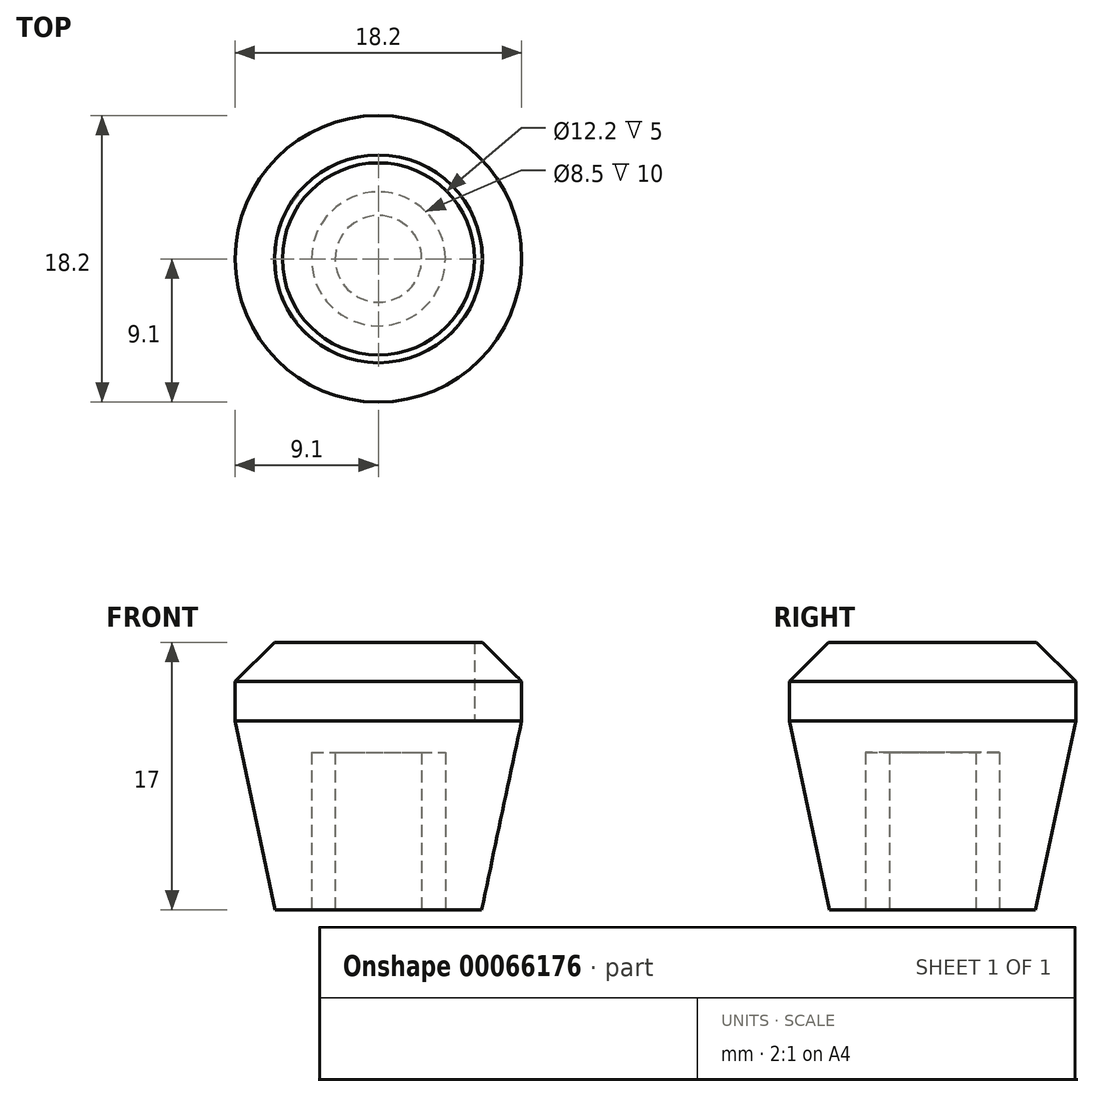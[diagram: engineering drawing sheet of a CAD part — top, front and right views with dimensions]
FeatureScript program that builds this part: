
annotation { "Feature Type Name" : "Feature", "Feature Type Description" : "" }
export const myFeature = defineFeature(function(context is Context, id is Id, definition is map)
    precondition{}
    {
        {
            assignVariable(context, id + "F0", {"variableType" : VariableType.NUMBER, "name" : "magt", "numberValue" : 5});
        }
        {
            var Q0;
            Q0=qCreatedBy(makeId("Top.planeOp"),FACE);
            var sketch = newSketch(context, id + "F1", { "sketchPlane" : qUnion([Q0])});
            skCircle(sketch, "E0", {"center": v(0, 0) * mm, "radius": 6.1 * mm});
            skCircle(sketch, "E1", {"center": v(0, 0) * mm, "radius": 9.1 * mm});
            skSolve(sketch);
        }
        {
            var Q0;
            Q0=makeQuery(id+"F1.imprint","IMPRINT",FACE,{"disambiguationData":[TD([[makeQuery(id+"F1.imprint","IMPRINT",EDGE,{"derivedFrom":sQuery(id+"F1.wireOp",EDGE,"E0")}),-1.0]])]});
            extrude(context, id + "F2", {"entities" : qUnion([Q0]), "depth" : getVariable(context, 'magt') * mm, "offsetDistance" : 25 * mm});
        }
        {
            var Q0;
            Q0=makeQuery(id+"F1.imprint","IMPRINT",FACE,{"disambiguationData":[TD([[makeQuery(id+"F1.imprint","IMPRINT",EDGE,{"derivedFrom":sQuery(id+"F1.wireOp",EDGE,"E0")}),-1.0]])]});
            var Q1;
            Q1=makeQuery(id+"F1.imprint","IMPRINT",FACE,{"disambiguationData":[TD([[makeQuery(id+"F1.imprint","IMPRINT",EDGE,{"derivedFrom":sQuery(id+"F1.wireOp",EDGE,"E0")}),1.0]])]});
            extrude(context, id + "F3", {"entities" : qUnion([Q0, Q1]), "operationType" : NewBodyOperationType.ADD, "oppositeDirection" : true, "depth" : 12 * mm, "offsetDistance" : 25 * mm, "hasDraft" : true, "draftAngle" : 12 * degree, "draftPullDirection" : true});
        }
        {
            var Q0;
            Q0=makeQuery(id+"F3.opExtrude","CAP_FACE",FACE,{"disambiguationData":[OSD([sQuery(id+"F1.wireOp",EDGE,"E1")])],"isStart":false});
            var sketch = newSketch(context, id + "F4", { "sketchPlane" : qUnion([Q0])});
            skCircle(sketch, "E2", {"center": v(0, 0) * mm, "radius": 4.25 * mm});
            skCircle(sketch, "E3", {"center": v(0, 0) * mm, "radius": 2.75 * mm});
            skSolve(sketch);
        }
        {
            var Q0;
            Q0 = qSketchRegion(id + "F4", true);
            extrude(context, id + "F5", {"entities" : qUnion([Q0]), "operationType" : NewBodyOperationType.REMOVE, "oppositeDirection" : true, "depth" : 10 * mm, "offsetDistance" : 25 * mm});
        }
        {
            var Q0;
            Q0=makeQuery(id+"F2.opExtrude","CAP_EDGE",EDGE,{"disambiguationData":[OSD([sQuery(id+"F1.wireOp",EDGE,"E1")])],"isStart":false});
            chamfer(context, id + "F6", {"entities" : qUnion([Q0]), "width" : 2.5 * mm, "tangentPropagation" : true});
        }
    });
